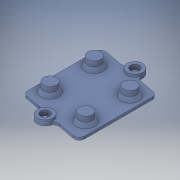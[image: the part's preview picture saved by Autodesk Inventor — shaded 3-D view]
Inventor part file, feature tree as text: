
AUTODESK INVENTOR PART (.ipt)
format: ipt  version: 2019 (Build 230136000, 136)  size: 215,552 bytes
history: native  units: mm
features: extrude x4, chamfer x4, sketch x4, fillet x2
ambient origin geometry x8: Origin, YZ Plane, XZ Plane, XY Plane, X Axis, Y Axis, Z Axis, Center Point
bodies: Solide1 (feature_tree)
feature tree (14):
  extrude  "Extrusion1"  Depth=30.0mm
  extrude  "Extrusion2"  Depth=26.0mm
  fillet  "Congé1"  Radius=13.0mm
  fillet  "Congé2"  Radius=5.0mm
  extrude  "Extrusion3"  Depth=30.0mm
  extrude  "Extrusion4"  Depth=1.0mm TaperAngle=0.0deg
  chamfer  "Chanfrein1"  Distance=3.5mm
  chamfer  "Chanfrein2"  Distance=3.5mm
  chamfer  "Chanfrein3"  Distance=36.0mm
  chamfer  "Chanfrein4"  Distance=12.5mm
  sketch  "Esquisse2"
  sketch  "Esquisse3"
  sketch  "Esquisse4"
  sketch  "Esquisse5"
